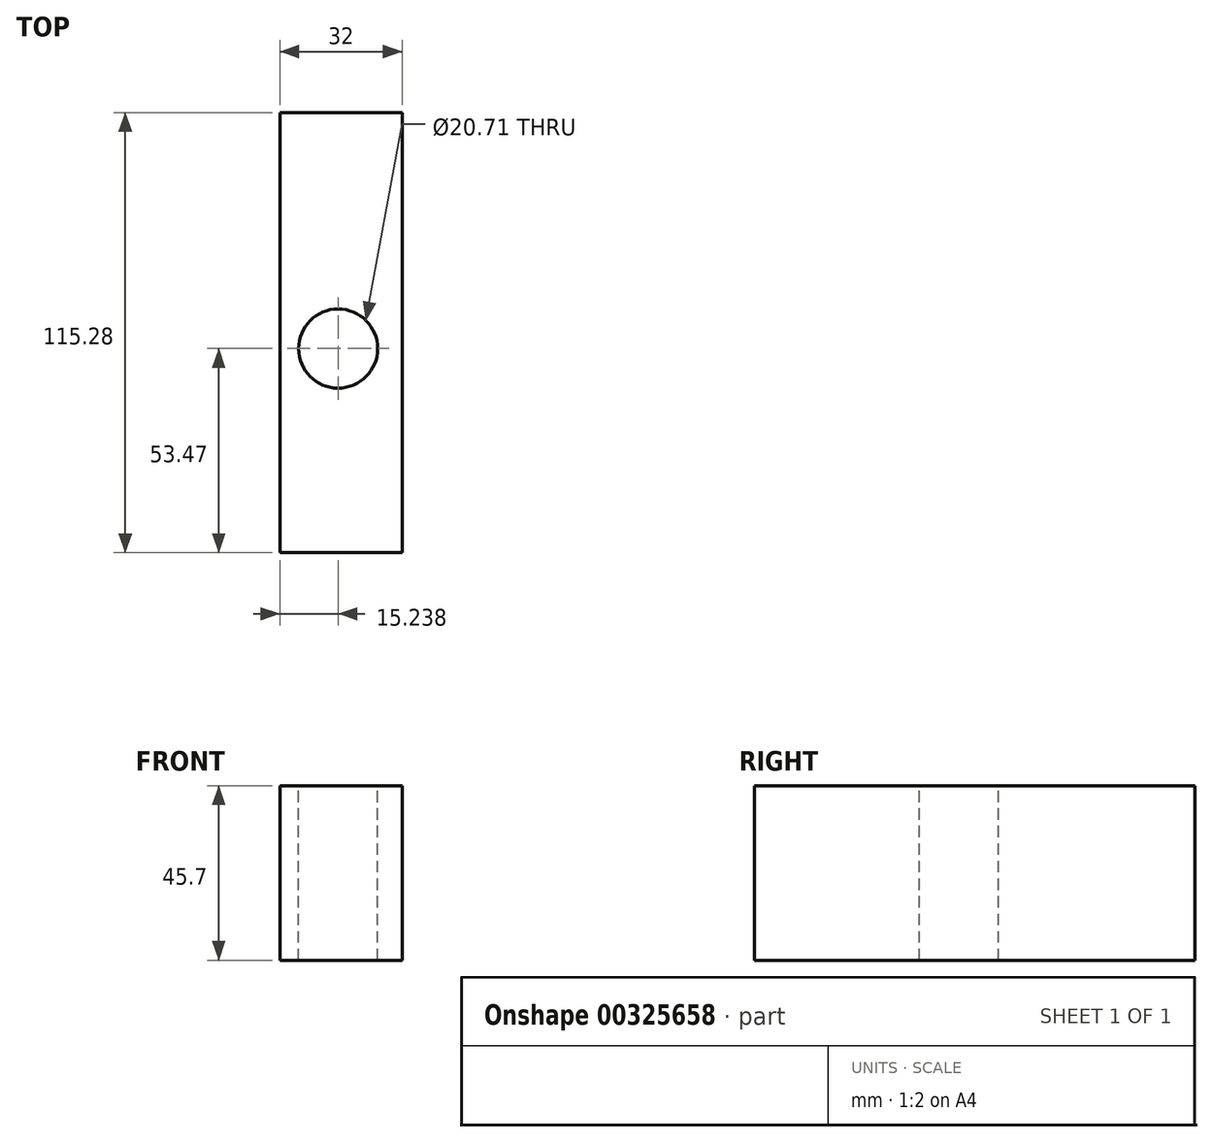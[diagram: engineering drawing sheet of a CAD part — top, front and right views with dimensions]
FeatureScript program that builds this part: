
annotation { "Feature Type Name" : "Feature", "Feature Type Description" : "" }
export const myFeature = defineFeature(function(context is Context, id is Id, definition is map)
    precondition{}
    {
        {
            var Q0;
            Q0=qCreatedBy(makeId("Right.planeOp"),FACE);
            var sketch = newSketch(context, id + "F0", { "sketchPlane" : qUnion([Q0])});
            skLineSegment(sketch, "E0.bottom", {"start": v(-53.47, 39.25) * mm, "end": v(61.8, 39.25) * mm});
            skLineSegment(sketch, "E0.top", {"start": v(-53.47, -6.45) * mm, "end": v(61.8, -6.45) * mm});
            skLineSegment(sketch, "E0.left", {"start": v(-53.47, 39.25) * mm, "end": v(-53.47, -6.45) * mm});
            skLineSegment(sketch, "E0.right", {"start": v(61.8, 39.25) * mm, "end": v(61.8, -6.45) * mm});
            skSolve(sketch);
        }
        {
            var Q0;
            Q0=makeQuery(id+"F0.imprint","IMPRINT",FACE,{"disambiguationData":[TD([[makeQuery(id+"F0.imprint","IMPRINT",EDGE,{"derivedFrom":sQuery(id+"F0.wireOp",EDGE,"E0.bottom")}),-1.0]])]});
            extrude(context, id + "F1", {"entities" : qUnion([Q0]), "depth" : 32 * mm});
        }
        {
            var Q0;
            Q0=makeQuery(id+"F1.opExtrude","SWEPT_FACE",FACE,{"disambiguationData":[OSD([sQuery(id+"F0.wireOp",EDGE,"E0.bottom")])]});
            var sketch = newSketch(context, id + "F2", { "sketchPlane" : qUnion([Q0])});
            skCircle(sketch, "E1", {"center": v(15.24, 0) * mm, "radius": 10.36 * mm});
            skSolve(sketch);
        }
        {
            var Q0;
            Q0=makeQuery(id+"F2.imprint","IMPRINT",FACE,{"disambiguationData":[TD([[makeQuery(id+"F2.imprint","IMPRINT",EDGE,{"derivedFrom":sQuery(id+"F2.wireOp",EDGE,"E1")}),1.0]])]});
            var Q1;
            Q1=makeQuery(id+"F1.opExtrude","SWEPT_FACE",FACE,{"disambiguationData":[OSD([sQuery(id+"F0.wireOp",EDGE,"E0.top")])]});
            extrude(context, id + "F3", {"entities" : qUnion([Q0]), "operationType" : NewBodyOperationType.REMOVE, "endBound" : BoundingType.UP_TO_SURFACE, "oppositeDirection" : true, "endBoundEntityFace" : qUnion([Q1]), "depth" : 25.4 * mm});
        }
    });
